# Revit family: Ghent - Slide Changeable Glassboard
name_source: partatom
category: Generic Models
units: mm (PartAtom-declared; Revit-internal decimal feet)

## family parameters
Can host rebar = No
Cut with Voids When Loaded = No
Host = Face
Part Type = Normal
Room Calculation Point = No
Round Connector Dimension = Use Diameter
Shared = No

## types (9) — shared parameters
Default Elevation = 4' - 0"
Glassboard = <By Category>
Hardware = <By Category>
Insert = <By Category>
Manufacturer = Ghent
URL = https://ghent.com
zero-valued in all types: Insert Slide Percentage (0-100)

## per-type parameters (varying)
| type | Height | Model | Width |
| 18"W x 24"H | 2' - 0" | GGINHMY18-FM-XXV | 1' - 6" |
| 24"W x 18"H | 1' - 6" | GGINHMY18-FM-XXH | 2' - 0" |
| 12"W x 16"H | 1' - 4" | GGINHMY1216-FM-XXV | 1' - 0" |
| 16"W x 12"H | 1' - 0" | GGINHMY1216-FM-XXH | 1' - 4" |
| 24"W x 24"H | 2' - 0" | GGINHMY2424-FM-XXH | 2' - 0" |
| 24"W x 30"H | 2' - 6" | GGINHMY2430-FM-XXV | 2' - 0" |
| 30"W x 24"H | 2' - 0" | GGINHMY2430-FM-XXH | 2' - 6" |
| 24"W x 36"H | 3' - 0" | GGINHMY23-FM-XXV | 2' - 0" |
| 36"W x 24"H | 2' - 0" | GGINHMY23-FM-XXH | 3' - 0" |

## geometry (parser evidence)
native form markers: Sweep x6
no freeform markers — native parametric forms only
